# Revit family: Control_Panels-Lutron-PD4-16-F(-CE)
name_source: partatom
category: Electrical Equipment
revit_build: Autodesk Revit 2017 (Build: 20160225_1515(x64)
units: mm (PartAtom-declared; Revit-internal decimal feet)

## family parameters
Cut with Voids When Loaded = No
Host = Face
OmniClass Number = 23.80.30.11.17
OmniClass Title = Distribution Boards and Control Panels
Panel Configuration = Two Columns, Circuits Across
Part Type = Panelboard
Room Calculation Point = No
Round Connector Dimension = Use Radius
Shared = No

## types (2) — shared parameters
Assembly Code = D5020200
Constraints = 1
Description = The Lutron myRoom and HomeWorks QS families of DIN rail panels are designed to accept DIN Power Modules (DPMs). The DPMs can be configured in the panel to control multiple load types to fit the size, lighting plan and design of the space.
Finish = Steel - Lutron - Black
Frequency = 50 Hz
Ground Bus = No
Instruction Sheet Link = http://www.lutron.com
Load Classification = Power
MCB Rating = 1 A
Manufacturer = Lutron Electronics Co., Inc
Manufacturer Fax Number = 610-282-1243
Neutral Bus = No
Neutral Rating = 0.00%
Number of Poles = 1
Overall Depth = 2.936 "
Overall Height = 16.128 "
Overall Width = 18.082 "
Performance URL = http://www.lutron.com
Phase = 1
Power Factor = 1
Product Documentation Link = http://www.lutron.com
Product Name = DIN Panels
Product Page URL = http://www.lutron.com
Series = myRoom
SubFeed Lugs = No
URL = http://www.lutron.com
Unit Weight = 30.00 lb
Version = 2017 - v1.0a
Video Link = https://www.youtube.com
Warranty URL = http://www.lutron.com
zero-valued in all types: Cost, Default Elevation

## per-type parameters (varying)
| type | Electrical Potential | Feed Through Control Circuit Voltage | Type Comments | Voltage |
| PD4-16-F | 120 V | 120 V | 120–240 V~ Non-CE High-Voltage Enclosure | 120–240 V~ 50/60 Hz |
| PD4-16-F-CE | 220 V | 220 V | 220-240 V~ CE High-Voltage Enclosure | 220-240 V~ 50/60 Hz |

note: column(s) folded — value = type name in every type: Model

## geometry (parser evidence)
native form markers: Sweep x2
no freeform markers — native parametric forms only
